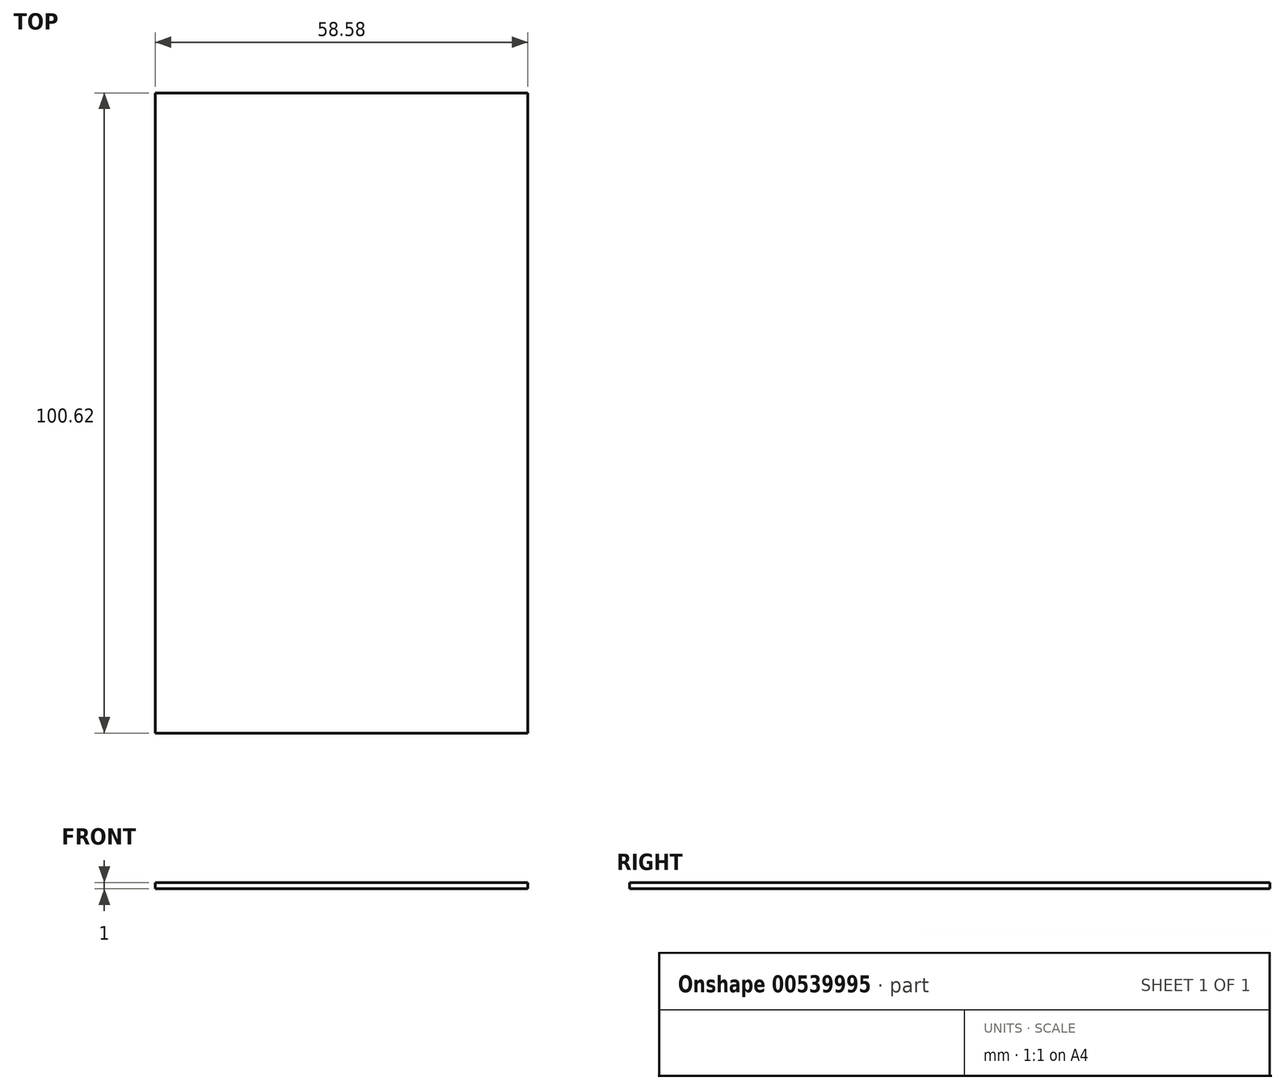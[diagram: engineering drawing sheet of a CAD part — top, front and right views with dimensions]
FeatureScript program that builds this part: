
annotation { "Feature Type Name" : "Feature", "Feature Type Description" : "" }
export const myFeature = defineFeature(function(context is Context, id is Id, definition is map)
    precondition{}
    {
        {
            var Q0;
            Q0=qCreatedBy(makeId("Top.planeOp"),FACE);
            var sketch = newSketch(context, id + "F0", { "sketchPlane" : qUnion([Q0])});
            skLineSegment(sketch, "E0.bottom", {"start": v(29.29, -50.31) * mm, "end": v(-29.28, -50.31) * mm});
            skLineSegment(sketch, "E0.top", {"start": v(29.28, 50.31) * mm, "end": v(-29.29, 50.31) * mm});
            skLineSegment(sketch, "E0.left", {"start": v(29.29, -50.31) * mm, "end": v(29.28, 50.32) * mm});
            skLineSegment(sketch, "E0.right", {"start": v(-29.28, -50.31) * mm, "end": v(-29.29, 50.32) * mm});
            skPoint(sketch, "E0.middle", {"position": v(0, 0) * mm});
            skSolve(sketch);
        }
        {
            var Q0;
            Q0 = qSketchRegion(id + "F0", true);
            extrude(context, id + "F1", {"entities" : qUnion([Q0]), "depth" : 1 * mm, "offsetDistance" : 25 * mm});
        }
    });
